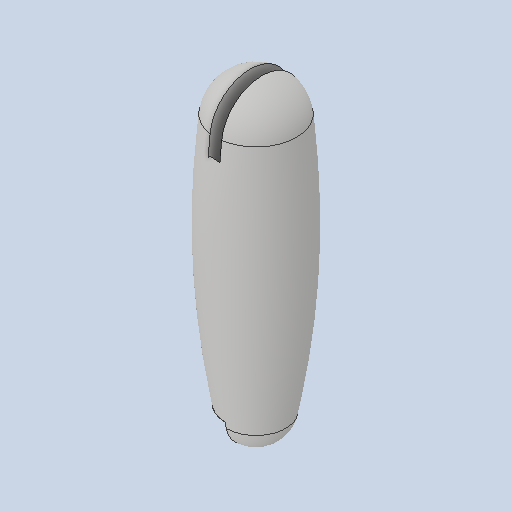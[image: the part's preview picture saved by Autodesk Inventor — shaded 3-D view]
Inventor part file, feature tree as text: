
AUTODESK INVENTOR PART (.ipt)
format: ipt  version: 2024.2 (Build 282272000, 272)  size: 156,160 bytes
history: native  units: mm
features: sketch x4, revolve x2, extrude x2, other x1
ambient origin geometry x8: Origin, YZ Plane, XZ Plane, XY Plane, X Axis, Y Axis, Z Axis, Center Point
bodies: Body1 (feature_tree)
feature tree (9):
  other  "Твердое тело1"
  revolve  "Вращение1"
  extrude  "Выдавливание1"  Depth=140.0mm
  revolve  "Вращение2"
  extrude  "Выдавливание2"  Depth=104.0mm
  sketch  "Эскиз1"
  sketch  "Эскиз2"
  sketch  "Эскиз3"
  sketch  "Эскиз4"
